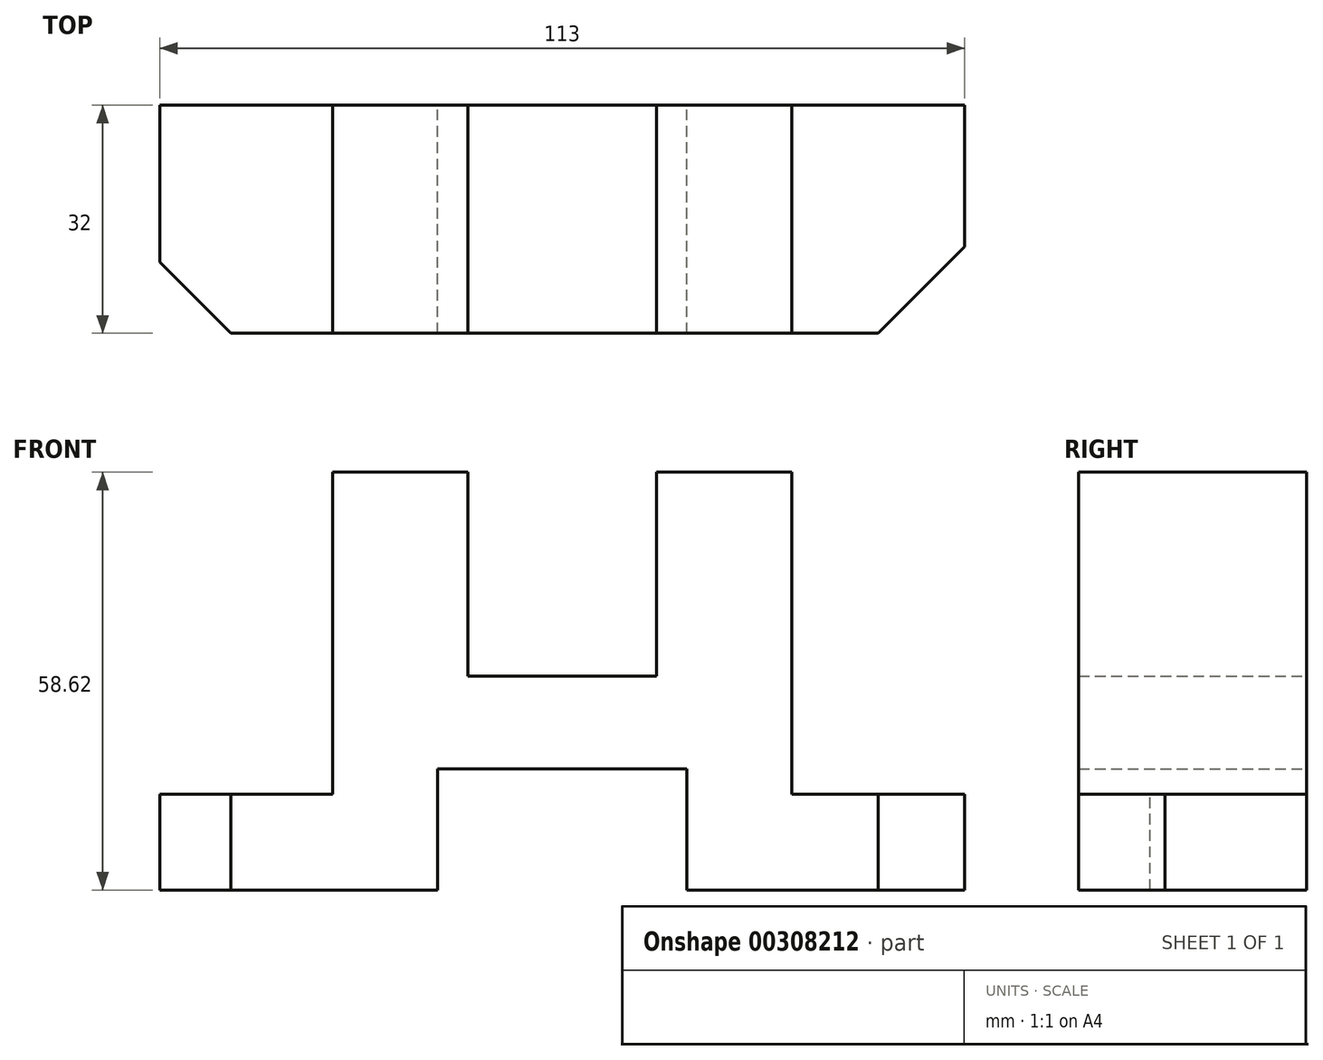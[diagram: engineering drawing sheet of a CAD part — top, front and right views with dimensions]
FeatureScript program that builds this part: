
annotation { "Feature Type Name" : "Feature", "Feature Type Description" : "" }
export const myFeature = defineFeature(function(context is Context, id is Id, definition is map)
    precondition{}
    {
        {
            var Q0;
            Q0=qCreatedBy(makeId("Front.planeOp"),FACE);
            var sketch = newSketch(context, id + "F0", { "sketchPlane" : qUnion([Q0])});
            skLineSegment(sketch, "E0", {"start": v(-56.5, 0) * mm, "end": v(-17.5, 0) * mm});
            skLineSegment(sketch, "E1", {"start": v(-17.5, 0) * mm, "end": v(-17.5, 17) * mm});
            skLineSegment(sketch, "E2", {"start": v(-17.5, 17) * mm, "end": v(17.5, 17) * mm});
            skLineSegment(sketch, "E3", {"start": v(17.5, 17) * mm, "end": v(17.5, 0) * mm});
            skLineSegment(sketch, "E4", {"start": v(17.5, 0) * mm, "end": v(56.5, 0) * mm});
            skLineSegment(sketch, "E5", {"start": v(56.5, 0) * mm, "end": v(56.5, 13.42) * mm});
            skLineSegment(sketch, "E6", {"start": v(56.5, 13.42) * mm, "end": v(32.23, 13.42) * mm});
            skLineSegment(sketch, "E7", {"start": v(32.23, 13.42) * mm, "end": v(32.23, 58.62) * mm});
            skLineSegment(sketch, "E8", {"start": v(32.23, 58.62) * mm, "end": v(13.23, 58.62) * mm});
            skLineSegment(sketch, "E9", {"start": v(13.23, 58.62) * mm, "end": v(13.23, 30) * mm});
            skLineSegment(sketch, "E10", {"start": v(13.23, 30) * mm, "end": v(-13.23, 30) * mm});
            skLineSegment(sketch, "E11", {"start": v(-13.23, 30) * mm, "end": v(-13.23, 58.62) * mm});
            skLineSegment(sketch, "E12", {"start": v(-13.23, 58.62) * mm, "end": v(-32.23, 58.62) * mm});
            skLineSegment(sketch, "E13", {"start": v(-32.23, 58.62) * mm, "end": v(-32.23, 13.42) * mm});
            skLineSegment(sketch, "E14", {"start": v(-32.23, 13.42) * mm, "end": v(-56.5, 13.42) * mm});
            skLineSegment(sketch, "E15", {"start": v(-56.5, 13.42) * mm, "end": v(-56.5, 0) * mm});
            skLineSegment(sketch, "E16", {"start": v(-17.5, 0) * mm, "end": v(17.5, 0) * mm, "construction": true});
            skSolve(sketch);
        }
        {
            var Q0;
            Q0 = qSketchRegion(id + "F0", true);
            extrude(context, id + "F1", {"entities" : qUnion([Q0]), "depth" : 32 * mm});
        }
        {
            var Q0;
            Q0=makeQuery(id+"F1.opExtrude","SWEPT_FACE",FACE,{"disambiguationData":[OSD([sQuery(id+"F0.wireOp",EDGE,"E14")])]});
            var sketch = newSketch(context, id + "F2", { "sketchPlane" : qUnion([Q0])});
            skLineSegment(sketch, "E17", {"start": v(-46.5, -32) * mm, "end": v(-56.5, -32) * mm});
            skLineSegment(sketch, "E18", {"start": v(-56.5, -32) * mm, "end": v(-56.5, -22) * mm});
            skLineSegment(sketch, "E19", {"start": v(-56.5, -22) * mm, "end": v(-46.5, -32) * mm});
            skSolve(sketch);
        }
        {
            var Q0;
            Q0 = qSketchRegion(id + "F2", true);
            extrude(context, id + "F3", {"entities" : qUnion([Q0]), "operationType" : NewBodyOperationType.REMOVE, "endBound" : BoundingType.THROUGH_ALL, "oppositeDirection" : true, "depth" : 25 * mm});
        }
        {
            var Q0;
            Q0=makeQuery(id+"F1.opExtrude","SWEPT_FACE",FACE,{"disambiguationData":[OSD([sQuery(id+"F0.wireOp",EDGE,"E6")])]});
            var sketch = newSketch(context, id + "F4", { "sketchPlane" : qUnion([Q0])});
            skLineSegment(sketch, "E20", {"start": v(44.36, -32) * mm, "end": v(56.5, -19.86) * mm});
            skLineSegment(sketch, "E21", {"start": v(56.5, -19.86) * mm, "end": v(56.5, -32) * mm});
            skLineSegment(sketch, "E22", {"start": v(56.5, -32) * mm, "end": v(44.36, -32) * mm});
            skSolve(sketch);
        }
        {
            var Q0;
            Q0=makeQuery(id+"F4.imprint","IMPRINT",FACE,{"disambiguationData":[TD([[makeQuery(id+"F4.imprint","IMPRINT",EDGE,{"derivedFrom":sQuery(id+"F4.wireOp",EDGE,"E20")}),-1.0]])]});
            extrude(context, id + "F5", {"entities" : qUnion([Q0]), "operationType" : NewBodyOperationType.REMOVE, "endBound" : BoundingType.THROUGH_ALL, "oppositeDirection" : true, "depth" : 25 * mm});
        }
    });
